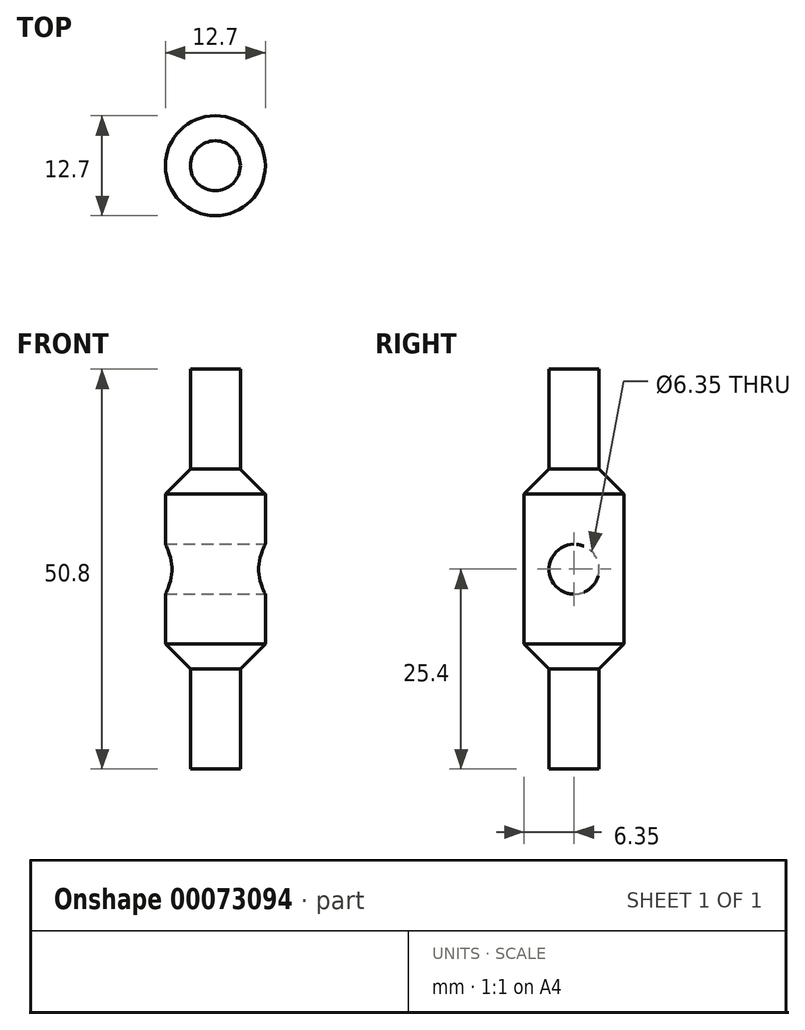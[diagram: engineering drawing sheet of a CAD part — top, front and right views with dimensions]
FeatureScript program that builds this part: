
annotation { "Feature Type Name" : "Feature", "Feature Type Description" : "" }
export const myFeature = defineFeature(function(context is Context, id is Id, definition is map)
    precondition{}
    {
        {
            var Q0;
            Q0=qCreatedBy(makeId("Top.planeOp"),FACE);
            var sketch = newSketch(context, id + "F0", { "sketchPlane" : qUnion([Q0])});
            skCircle(sketch, "E0", {"center": v(0, 0) * mm, "radius": 6.35 * mm});
            skSolve(sketch);
        }
        {
            var Q0;
            Q0 = qSketchRegion(id + "F0", true);
            extrude(context, id + "F1", {"entities" : qUnion([Q0]), "endBound" : BoundingType.SYMMETRIC, "depth" : 25.4 * mm});
        }
        {
            var Q0;
            Q0=qCreatedBy(makeId("Top.planeOp"),FACE);
            var sketch = newSketch(context, id + "F2", { "sketchPlane" : qUnion([Q0])});
            skCircle(sketch, "E1", {"center": v(0, 0) * mm, "radius": 3.18 * mm});
            skSolve(sketch);
        }
        {
            var Q0;
            Q0=makeQuery(id+"F2.imprint","IMPRINT",FACE,{"disambiguationData":[TD([[makeQuery(id+"F2.imprint","IMPRINT",EDGE,{"derivedFrom":sQuery(id+"F2.wireOp",EDGE,"E1")}),1.0]])]});
            extrude(context, id + "F3", {"entities" : qUnion([Q0]), "operationType" : NewBodyOperationType.ADD, "endBound" : BoundingType.SYMMETRIC, "depth" : 50.8 * mm});
        }
        {
            var Q0;
            Q0=makeQuery(id+"F1.opExtrude","CAP_EDGE",EDGE,{"disambiguationData":[OSD([sQuery(id+"F0.wireOp",EDGE,"E0")])],"isStart":true});
            var Q1;
            Q1=makeQuery(id+"F1.opExtrude","CAP_EDGE",EDGE,{"disambiguationData":[OSD([sQuery(id+"F0.wireOp",EDGE,"E0")])],"isStart":false});
            chamfer(context, id + "F4", {"entities" : qUnion([Q0, Q1]), "width" : 3.17 * mm, "tangentPropagation" : true});
        }
        {
            var Q0;
            Q0=qCreatedBy(makeId("Right.planeOp"),FACE);
            var sketch = newSketch(context, id + "F5", { "sketchPlane" : qUnion([Q0])});
            skCircle(sketch, "E2", {"center": v(0, 0) * mm, "radius": 3.18 * mm});
            skSolve(sketch);
        }
        {
            var Q0;
            Q0 = qSketchRegion(id + "F5", true);
            extrude(context, id + "F6", {"entities" : qUnion([Q0]), "operationType" : NewBodyOperationType.REMOVE, "endBound" : BoundingType.SYMMETRIC, "oppositeDirection" : true, "depth" : 25.4 * mm});
        }
    });
